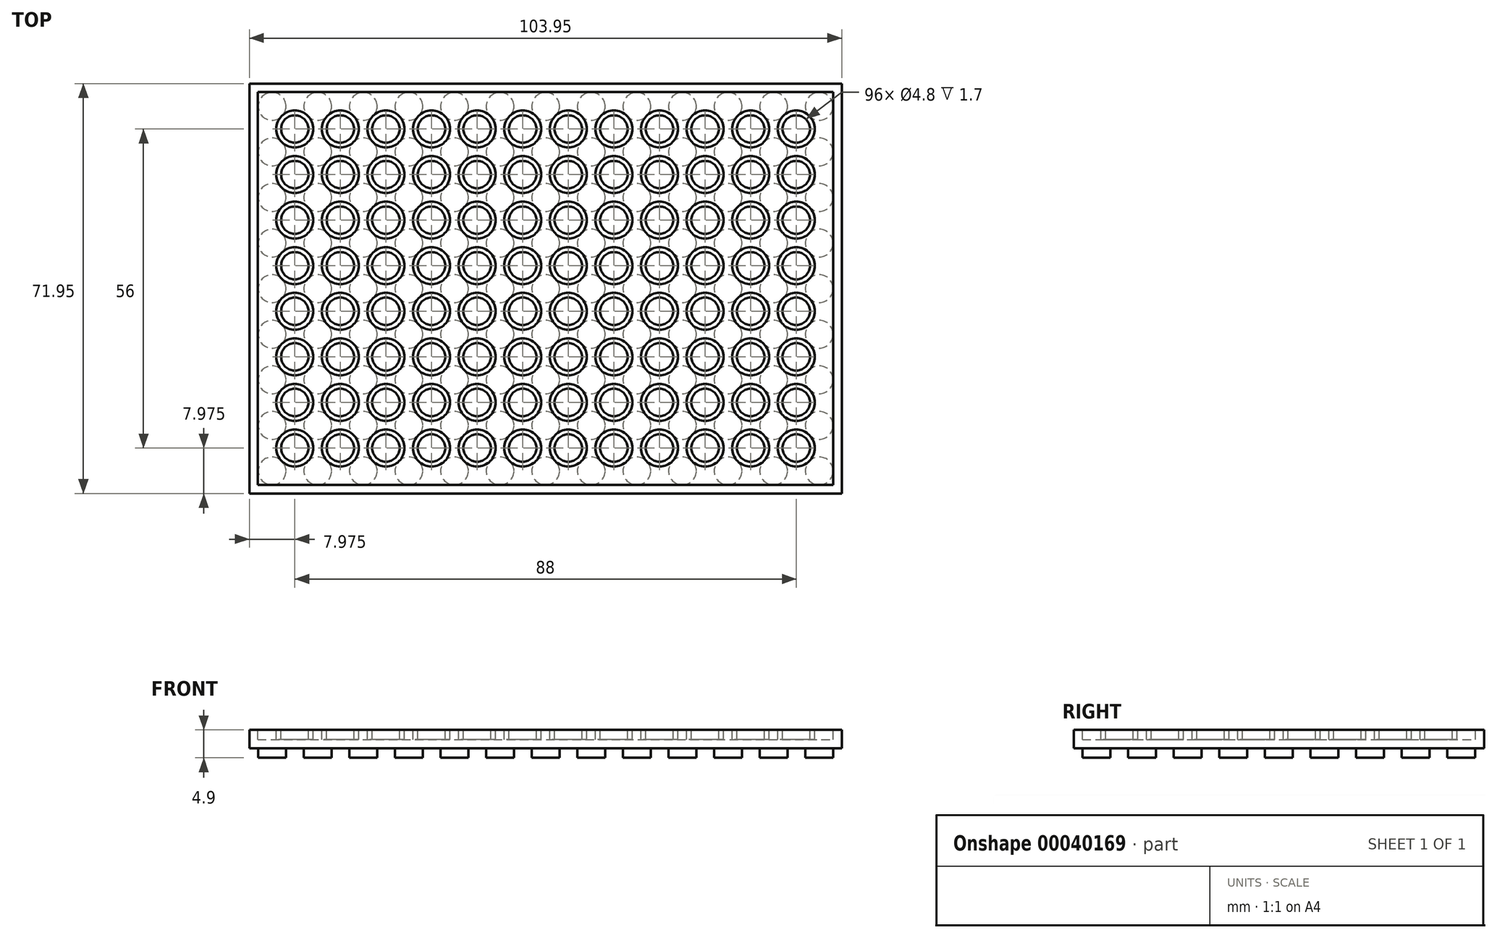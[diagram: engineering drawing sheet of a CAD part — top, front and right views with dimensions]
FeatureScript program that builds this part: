
annotation { "Feature Type Name" : "Feature", "Feature Type Description" : "" }
export const myFeature = defineFeature(function(context is Context, id is Id, definition is map)
    precondition{}
    {
        {
            var Q0;
            Q0=qCreatedBy(makeId("Top.planeOp"),FACE);
            var sketch = newSketch(context, id + "F0", { "sketchPlane" : qUnion([Q0])});
            skLineSegment(sketch, "E0.bottom", {"start": v(0, 0) * mm, "end": v(-103.95, 0) * mm});
            skLineSegment(sketch, "E0.top", {"start": v(0, 71.95) * mm, "end": v(-103.95, 71.95) * mm});
            skLineSegment(sketch, "E0.left", {"start": v(0, 0) * mm, "end": v(0, 71.95) * mm});
            skLineSegment(sketch, "E0.right", {"start": v(-103.95, 0) * mm, "end": v(-103.95, 71.95) * mm});
            skSolve(sketch);
        }
        {
            var Q0;
            Q0=makeQuery(id+"F0.imprint","IMPRINT",FACE,{"disambiguationData":[TD([[makeQuery(id+"F0.imprint","IMPRINT",EDGE,{"derivedFrom":sQuery(id+"F0.wireOp",EDGE,"E0.bottom")}),-1.0]])]});
            extrude(context, id + "F1", {"entities" : qUnion([Q0]), "oppositeDirection" : true, "depth" : 3.2 * mm});
        }
        {
            var Q0;
            Q0=qCreatedBy(makeId("Top.planeOp"),FACE);
            var sketch = newSketch(context, id + "F2", { "sketchPlane" : qUnion([Q0])});
            skLineSegment(sketch, "E1.bottom", {"start": v(-102.47, 1.47) * mm, "end": v(-1.47, 1.48) * mm});
            skLineSegment(sketch, "E1.top", {"start": v(-102.48, 70.47) * mm, "end": v(-1.48, 70.47) * mm});
            skLineSegment(sketch, "E1.left", {"start": v(-102.47, 1.47) * mm, "end": v(-102.48, 70.47) * mm});
            skLineSegment(sketch, "E1.right", {"start": v(-1.47, 1.48) * mm, "end": v(-1.48, 70.47) * mm});
            skCircle(sketch, "E2", {"center": v(-7.97, 7.98) * mm, "radius": 3.25 * mm});
            skCircle(sketch, "E3.0.1.0", {"center": v(-7.97, 15.98) * mm, "radius": 3.25 * mm});
            skCircle(sketch, "E3.0.2.0", {"center": v(-7.97, 23.98) * mm, "radius": 3.25 * mm});
            skCircle(sketch, "E3.0.3.0", {"center": v(-7.97, 31.98) * mm, "radius": 3.25 * mm});
            skCircle(sketch, "E3.0.4.0", {"center": v(-7.97, 39.98) * mm, "radius": 3.25 * mm});
            skCircle(sketch, "E3.0.5.0", {"center": v(-7.97, 47.98) * mm, "radius": 3.25 * mm});
            skCircle(sketch, "E3.0.6.0", {"center": v(-7.97, 55.98) * mm, "radius": 3.25 * mm});
            skCircle(sketch, "E3.0.7.0", {"center": v(-7.97, 63.98) * mm, "radius": 3.25 * mm});
            skCircle(sketch, "E3.1.0.0", {"center": v(-15.97, 7.98) * mm, "radius": 3.25 * mm});
            skCircle(sketch, "E3.1.1.0", {"center": v(-15.97, 15.98) * mm, "radius": 3.25 * mm});
            skCircle(sketch, "E3.1.2.0", {"center": v(-15.97, 23.98) * mm, "radius": 3.25 * mm});
            skCircle(sketch, "E3.1.3.0", {"center": v(-15.97, 31.98) * mm, "radius": 3.25 * mm});
            skCircle(sketch, "E3.1.4.0", {"center": v(-15.97, 39.98) * mm, "radius": 3.25 * mm});
            skCircle(sketch, "E3.1.5.0", {"center": v(-15.97, 47.98) * mm, "radius": 3.25 * mm});
            skCircle(sketch, "E3.1.6.0", {"center": v(-15.97, 55.98) * mm, "radius": 3.25 * mm});
            skCircle(sketch, "E3.1.7.0", {"center": v(-15.97, 63.98) * mm, "radius": 3.25 * mm});
            skCircle(sketch, "E3.2.0.0", {"center": v(-23.97, 7.98) * mm, "radius": 3.25 * mm});
            skCircle(sketch, "E3.2.1.0", {"center": v(-23.97, 15.98) * mm, "radius": 3.25 * mm});
            skCircle(sketch, "E3.2.2.0", {"center": v(-23.97, 23.98) * mm, "radius": 3.25 * mm});
            skCircle(sketch, "E3.2.3.0", {"center": v(-23.97, 31.98) * mm, "radius": 3.25 * mm});
            skCircle(sketch, "E3.2.4.0", {"center": v(-23.97, 39.98) * mm, "radius": 3.25 * mm});
            skCircle(sketch, "E3.2.5.0", {"center": v(-23.97, 47.98) * mm, "radius": 3.25 * mm});
            skCircle(sketch, "E3.2.6.0", {"center": v(-23.97, 55.98) * mm, "radius": 3.25 * mm});
            skCircle(sketch, "E3.2.7.0", {"center": v(-23.97, 63.98) * mm, "radius": 3.25 * mm});
            skCircle(sketch, "E3.3.0.0", {"center": v(-31.97, 7.98) * mm, "radius": 3.25 * mm});
            skCircle(sketch, "E3.3.1.0", {"center": v(-31.97, 15.98) * mm, "radius": 3.25 * mm});
            skCircle(sketch, "E3.3.2.0", {"center": v(-31.97, 23.98) * mm, "radius": 3.25 * mm});
            skCircle(sketch, "E3.3.3.0", {"center": v(-31.97, 31.98) * mm, "radius": 3.25 * mm});
            skCircle(sketch, "E3.3.4.0", {"center": v(-31.97, 39.98) * mm, "radius": 3.25 * mm});
            skCircle(sketch, "E3.3.5.0", {"center": v(-31.97, 47.98) * mm, "radius": 3.25 * mm});
            skCircle(sketch, "E3.3.6.0", {"center": v(-31.97, 55.98) * mm, "radius": 3.25 * mm});
            skCircle(sketch, "E3.3.7.0", {"center": v(-31.97, 63.98) * mm, "radius": 3.25 * mm});
            skCircle(sketch, "E3.4.0.0", {"center": v(-39.97, 7.98) * mm, "radius": 3.25 * mm});
            skCircle(sketch, "E3.4.1.0", {"center": v(-39.97, 15.98) * mm, "radius": 3.25 * mm});
            skCircle(sketch, "E3.4.2.0", {"center": v(-39.97, 23.98) * mm, "radius": 3.25 * mm});
            skCircle(sketch, "E3.4.3.0", {"center": v(-39.97, 31.98) * mm, "radius": 3.25 * mm});
            skCircle(sketch, "E3.4.4.0", {"center": v(-39.97, 39.98) * mm, "radius": 3.25 * mm});
            skCircle(sketch, "E3.4.5.0", {"center": v(-39.97, 47.98) * mm, "radius": 3.25 * mm});
            skCircle(sketch, "E3.4.6.0", {"center": v(-39.97, 55.98) * mm, "radius": 3.25 * mm});
            skCircle(sketch, "E3.4.7.0", {"center": v(-39.97, 63.98) * mm, "radius": 3.25 * mm});
            skCircle(sketch, "E3.5.0.0", {"center": v(-47.97, 7.98) * mm, "radius": 3.25 * mm});
            skCircle(sketch, "E3.5.1.0", {"center": v(-47.97, 15.98) * mm, "radius": 3.25 * mm});
            skCircle(sketch, "E3.5.2.0", {"center": v(-47.97, 23.98) * mm, "radius": 3.25 * mm});
            skCircle(sketch, "E3.5.3.0", {"center": v(-47.97, 31.98) * mm, "radius": 3.25 * mm});
            skCircle(sketch, "E3.5.4.0", {"center": v(-47.97, 39.98) * mm, "radius": 3.25 * mm});
            skCircle(sketch, "E3.5.5.0", {"center": v(-47.97, 47.98) * mm, "radius": 3.25 * mm});
            skCircle(sketch, "E3.5.6.0", {"center": v(-47.97, 55.98) * mm, "radius": 3.25 * mm});
            skCircle(sketch, "E3.5.7.0", {"center": v(-47.97, 63.98) * mm, "radius": 3.25 * mm});
            skCircle(sketch, "E3.6.0.0", {"center": v(-55.97, 7.98) * mm, "radius": 3.25 * mm});
            skCircle(sketch, "E3.6.1.0", {"center": v(-55.97, 15.98) * mm, "radius": 3.25 * mm});
            skCircle(sketch, "E3.6.2.0", {"center": v(-55.97, 23.98) * mm, "radius": 3.25 * mm});
            skCircle(sketch, "E3.6.3.0", {"center": v(-55.97, 31.98) * mm, "radius": 3.25 * mm});
            skCircle(sketch, "E3.6.4.0", {"center": v(-55.97, 39.98) * mm, "radius": 3.25 * mm});
            skCircle(sketch, "E3.6.5.0", {"center": v(-55.97, 47.98) * mm, "radius": 3.25 * mm});
            skCircle(sketch, "E3.6.6.0", {"center": v(-55.97, 55.98) * mm, "radius": 3.25 * mm});
            skCircle(sketch, "E3.6.7.0", {"center": v(-55.97, 63.98) * mm, "radius": 3.25 * mm});
            skCircle(sketch, "E3.7.0.0", {"center": v(-63.98, 7.98) * mm, "radius": 3.25 * mm});
            skCircle(sketch, "E3.7.1.0", {"center": v(-63.98, 15.98) * mm, "radius": 3.25 * mm});
            skCircle(sketch, "E3.7.2.0", {"center": v(-63.98, 23.98) * mm, "radius": 3.25 * mm});
            skCircle(sketch, "E3.7.3.0", {"center": v(-63.98, 31.98) * mm, "radius": 3.25 * mm});
            skCircle(sketch, "E3.7.4.0", {"center": v(-63.98, 39.98) * mm, "radius": 3.25 * mm});
            skCircle(sketch, "E3.7.5.0", {"center": v(-63.98, 47.98) * mm, "radius": 3.25 * mm});
            skCircle(sketch, "E3.7.6.0", {"center": v(-63.98, 55.98) * mm, "radius": 3.25 * mm});
            skCircle(sketch, "E3.7.7.0", {"center": v(-63.98, 63.98) * mm, "radius": 3.25 * mm});
            skCircle(sketch, "E3.8.0.0", {"center": v(-71.97, 7.98) * mm, "radius": 3.25 * mm});
            skCircle(sketch, "E3.8.1.0", {"center": v(-71.97, 15.98) * mm, "radius": 3.25 * mm});
            skCircle(sketch, "E3.8.2.0", {"center": v(-71.97, 23.98) * mm, "radius": 3.25 * mm});
            skCircle(sketch, "E3.8.3.0", {"center": v(-71.97, 31.98) * mm, "radius": 3.25 * mm});
            skCircle(sketch, "E3.8.4.0", {"center": v(-71.97, 39.98) * mm, "radius": 3.25 * mm});
            skCircle(sketch, "E3.8.5.0", {"center": v(-71.97, 47.98) * mm, "radius": 3.25 * mm});
            skCircle(sketch, "E3.8.6.0", {"center": v(-71.97, 55.98) * mm, "radius": 3.25 * mm});
            skCircle(sketch, "E3.8.7.0", {"center": v(-71.97, 63.98) * mm, "radius": 3.25 * mm});
            skCircle(sketch, "E3.9.0.0", {"center": v(-79.98, 7.98) * mm, "radius": 3.25 * mm});
            skCircle(sketch, "E3.9.1.0", {"center": v(-79.98, 15.98) * mm, "radius": 3.25 * mm});
            skCircle(sketch, "E3.9.2.0", {"center": v(-79.98, 23.98) * mm, "radius": 3.25 * mm});
            skCircle(sketch, "E3.9.3.0", {"center": v(-79.98, 31.98) * mm, "radius": 3.25 * mm});
            skCircle(sketch, "E3.9.4.0", {"center": v(-79.98, 39.98) * mm, "radius": 3.25 * mm});
            skCircle(sketch, "E3.9.5.0", {"center": v(-79.98, 47.98) * mm, "radius": 3.25 * mm});
            skCircle(sketch, "E3.9.6.0", {"center": v(-79.98, 55.98) * mm, "radius": 3.25 * mm});
            skCircle(sketch, "E3.9.7.0", {"center": v(-79.98, 63.98) * mm, "radius": 3.25 * mm});
            skCircle(sketch, "E3.10.0.0", {"center": v(-87.97, 7.98) * mm, "radius": 3.25 * mm});
            skCircle(sketch, "E3.10.1.0", {"center": v(-87.97, 15.98) * mm, "radius": 3.25 * mm});
            skCircle(sketch, "E3.10.2.0", {"center": v(-87.97, 23.98) * mm, "radius": 3.25 * mm});
            skCircle(sketch, "E3.10.3.0", {"center": v(-87.97, 31.98) * mm, "radius": 3.25 * mm});
            skCircle(sketch, "E3.10.4.0", {"center": v(-87.97, 39.98) * mm, "radius": 3.25 * mm});
            skCircle(sketch, "E3.10.5.0", {"center": v(-87.97, 47.98) * mm, "radius": 3.25 * mm});
            skCircle(sketch, "E3.10.6.0", {"center": v(-87.97, 55.98) * mm, "radius": 3.25 * mm});
            skCircle(sketch, "E3.10.7.0", {"center": v(-87.97, 63.98) * mm, "radius": 3.25 * mm});
            skCircle(sketch, "E3.11.0.0", {"center": v(-95.97, 7.98) * mm, "radius": 3.25 * mm});
            skCircle(sketch, "E3.11.1.0", {"center": v(-95.97, 15.98) * mm, "radius": 3.25 * mm});
            skCircle(sketch, "E3.11.2.0", {"center": v(-95.97, 23.98) * mm, "radius": 3.25 * mm});
            skCircle(sketch, "E3.11.3.0", {"center": v(-95.97, 31.98) * mm, "radius": 3.25 * mm});
            skCircle(sketch, "E3.11.4.0", {"center": v(-95.97, 39.98) * mm, "radius": 3.25 * mm});
            skCircle(sketch, "E3.11.5.0", {"center": v(-95.97, 47.98) * mm, "radius": 3.25 * mm});
            skCircle(sketch, "E3.11.6.0", {"center": v(-95.97, 55.98) * mm, "radius": 3.25 * mm});
            skCircle(sketch, "E3.11.7.0", {"center": v(-95.97, 63.98) * mm, "radius": 3.25 * mm});
            skLineSegment(sketch, "E3.direction1", {"start": v(-7.97, 7.98) * mm, "end": v(-15.97, 7.98) * mm, "construction": true});
            skLineSegment(sketch, "E3.direction2", {"start": v(-7.97, 7.98) * mm, "end": v(-7.97, 15.98) * mm, "construction": true});
            skSolve(sketch);
        }
        {
            var Q0;
            Q0=qCreatedBy(makeId("Top.planeOp"),FACE);
            var sketch = newSketch(context, id + "F3", { "sketchPlane" : qUnion([Q0])});
            skCircle(sketch, "E4", {"center": v(-7.97, 7.98) * mm, "radius": 2.4 * mm});
            skCircle(sketch, "E5.0.1.0", {"center": v(-7.97, 15.98) * mm, "radius": 2.4 * mm});
            skCircle(sketch, "E5.0.2.0", {"center": v(-7.97, 23.98) * mm, "radius": 2.4 * mm});
            skCircle(sketch, "E5.0.3.0", {"center": v(-7.97, 31.98) * mm, "radius": 2.4 * mm});
            skCircle(sketch, "E5.0.4.0", {"center": v(-7.97, 39.98) * mm, "radius": 2.4 * mm});
            skCircle(sketch, "E5.0.5.0", {"center": v(-7.97, 47.98) * mm, "radius": 2.4 * mm});
            skCircle(sketch, "E5.0.6.0", {"center": v(-7.97, 55.98) * mm, "radius": 2.4 * mm});
            skCircle(sketch, "E5.0.7.0", {"center": v(-7.97, 63.98) * mm, "radius": 2.4 * mm});
            skCircle(sketch, "E5.1.0.0", {"center": v(-15.97, 7.98) * mm, "radius": 2.4 * mm});
            skCircle(sketch, "E5.1.1.0", {"center": v(-15.97, 15.98) * mm, "radius": 2.4 * mm});
            skCircle(sketch, "E5.1.2.0", {"center": v(-15.97, 23.98) * mm, "radius": 2.4 * mm});
            skCircle(sketch, "E5.1.3.0", {"center": v(-15.97, 31.98) * mm, "radius": 2.4 * mm});
            skCircle(sketch, "E5.1.4.0", {"center": v(-15.97, 39.98) * mm, "radius": 2.4 * mm});
            skCircle(sketch, "E5.1.5.0", {"center": v(-15.97, 47.98) * mm, "radius": 2.4 * mm});
            skCircle(sketch, "E5.1.6.0", {"center": v(-15.97, 55.98) * mm, "radius": 2.4 * mm});
            skCircle(sketch, "E5.1.7.0", {"center": v(-15.97, 63.98) * mm, "radius": 2.4 * mm});
            skCircle(sketch, "E5.2.0.0", {"center": v(-23.97, 7.98) * mm, "radius": 2.4 * mm});
            skCircle(sketch, "E5.2.1.0", {"center": v(-23.97, 15.98) * mm, "radius": 2.4 * mm});
            skCircle(sketch, "E5.2.2.0", {"center": v(-23.97, 23.98) * mm, "radius": 2.4 * mm});
            skCircle(sketch, "E5.2.3.0", {"center": v(-23.97, 31.98) * mm, "radius": 2.4 * mm});
            skCircle(sketch, "E5.2.4.0", {"center": v(-23.97, 39.98) * mm, "radius": 2.4 * mm});
            skCircle(sketch, "E5.2.5.0", {"center": v(-23.97, 47.98) * mm, "radius": 2.4 * mm});
            skCircle(sketch, "E5.2.6.0", {"center": v(-23.97, 55.98) * mm, "radius": 2.4 * mm});
            skCircle(sketch, "E5.2.7.0", {"center": v(-23.97, 63.98) * mm, "radius": 2.4 * mm});
            skCircle(sketch, "E5.3.0.0", {"center": v(-31.97, 7.98) * mm, "radius": 2.4 * mm});
            skCircle(sketch, "E5.3.1.0", {"center": v(-31.97, 15.98) * mm, "radius": 2.4 * mm});
            skCircle(sketch, "E5.3.2.0", {"center": v(-31.97, 23.98) * mm, "radius": 2.4 * mm});
            skCircle(sketch, "E5.3.3.0", {"center": v(-31.97, 31.98) * mm, "radius": 2.4 * mm});
            skCircle(sketch, "E5.3.4.0", {"center": v(-31.97, 39.98) * mm, "radius": 2.4 * mm});
            skCircle(sketch, "E5.3.5.0", {"center": v(-31.97, 47.98) * mm, "radius": 2.4 * mm});
            skCircle(sketch, "E5.3.6.0", {"center": v(-31.97, 55.98) * mm, "radius": 2.4 * mm});
            skCircle(sketch, "E5.3.7.0", {"center": v(-31.97, 63.98) * mm, "radius": 2.4 * mm});
            skCircle(sketch, "E5.4.0.0", {"center": v(-39.97, 7.98) * mm, "radius": 2.4 * mm});
            skCircle(sketch, "E5.4.1.0", {"center": v(-39.97, 15.98) * mm, "radius": 2.4 * mm});
            skCircle(sketch, "E5.4.2.0", {"center": v(-39.97, 23.98) * mm, "radius": 2.4 * mm});
            skCircle(sketch, "E5.4.3.0", {"center": v(-39.97, 31.98) * mm, "radius": 2.4 * mm});
            skCircle(sketch, "E5.4.4.0", {"center": v(-39.97, 39.98) * mm, "radius": 2.4 * mm});
            skCircle(sketch, "E5.4.5.0", {"center": v(-39.97, 47.98) * mm, "radius": 2.4 * mm});
            skCircle(sketch, "E5.4.6.0", {"center": v(-39.97, 55.98) * mm, "radius": 2.4 * mm});
            skCircle(sketch, "E5.4.7.0", {"center": v(-39.97, 63.98) * mm, "radius": 2.4 * mm});
            skCircle(sketch, "E5.5.0.0", {"center": v(-47.97, 7.98) * mm, "radius": 2.4 * mm});
            skCircle(sketch, "E5.5.1.0", {"center": v(-47.97, 15.98) * mm, "radius": 2.4 * mm});
            skCircle(sketch, "E5.5.2.0", {"center": v(-47.97, 23.98) * mm, "radius": 2.4 * mm});
            skCircle(sketch, "E5.5.3.0", {"center": v(-47.97, 31.98) * mm, "radius": 2.4 * mm});
            skCircle(sketch, "E5.5.4.0", {"center": v(-47.97, 39.98) * mm, "radius": 2.4 * mm});
            skCircle(sketch, "E5.5.5.0", {"center": v(-47.97, 47.98) * mm, "radius": 2.4 * mm});
            skCircle(sketch, "E5.5.6.0", {"center": v(-47.97, 55.98) * mm, "radius": 2.4 * mm});
            skCircle(sketch, "E5.5.7.0", {"center": v(-47.97, 63.98) * mm, "radius": 2.4 * mm});
            skCircle(sketch, "E5.6.0.0", {"center": v(-55.97, 7.98) * mm, "radius": 2.4 * mm});
            skCircle(sketch, "E5.6.1.0", {"center": v(-55.97, 15.98) * mm, "radius": 2.4 * mm});
            skCircle(sketch, "E5.6.2.0", {"center": v(-55.97, 23.98) * mm, "radius": 2.4 * mm});
            skCircle(sketch, "E5.6.3.0", {"center": v(-55.97, 31.98) * mm, "radius": 2.4 * mm});
            skCircle(sketch, "E5.6.4.0", {"center": v(-55.97, 39.98) * mm, "radius": 2.4 * mm});
            skCircle(sketch, "E5.6.5.0", {"center": v(-55.97, 47.98) * mm, "radius": 2.4 * mm});
            skCircle(sketch, "E5.6.6.0", {"center": v(-55.97, 55.98) * mm, "radius": 2.4 * mm});
            skCircle(sketch, "E5.6.7.0", {"center": v(-55.97, 63.98) * mm, "radius": 2.4 * mm});
            skCircle(sketch, "E5.7.0.0", {"center": v(-63.98, 7.98) * mm, "radius": 2.4 * mm});
            skCircle(sketch, "E5.7.1.0", {"center": v(-63.98, 15.98) * mm, "radius": 2.4 * mm});
            skCircle(sketch, "E5.7.2.0", {"center": v(-63.98, 23.98) * mm, "radius": 2.4 * mm});
            skCircle(sketch, "E5.7.3.0", {"center": v(-63.98, 31.98) * mm, "radius": 2.4 * mm});
            skCircle(sketch, "E5.7.4.0", {"center": v(-63.98, 39.98) * mm, "radius": 2.4 * mm});
            skCircle(sketch, "E5.7.5.0", {"center": v(-63.98, 47.98) * mm, "radius": 2.4 * mm});
            skCircle(sketch, "E5.7.6.0", {"center": v(-63.98, 55.98) * mm, "radius": 2.4 * mm});
            skCircle(sketch, "E5.7.7.0", {"center": v(-63.98, 63.98) * mm, "radius": 2.4 * mm});
            skCircle(sketch, "E5.8.0.0", {"center": v(-71.97, 7.98) * mm, "radius": 2.4 * mm});
            skCircle(sketch, "E5.8.1.0", {"center": v(-71.97, 15.98) * mm, "radius": 2.4 * mm});
            skCircle(sketch, "E5.8.2.0", {"center": v(-71.97, 23.98) * mm, "radius": 2.4 * mm});
            skCircle(sketch, "E5.8.3.0", {"center": v(-71.97, 31.98) * mm, "radius": 2.4 * mm});
            skCircle(sketch, "E5.8.4.0", {"center": v(-71.97, 39.98) * mm, "radius": 2.4 * mm});
            skCircle(sketch, "E5.8.5.0", {"center": v(-71.97, 47.98) * mm, "radius": 2.4 * mm});
            skCircle(sketch, "E5.8.6.0", {"center": v(-71.97, 55.98) * mm, "radius": 2.4 * mm});
            skCircle(sketch, "E5.8.7.0", {"center": v(-71.97, 63.98) * mm, "radius": 2.4 * mm});
            skCircle(sketch, "E5.9.0.0", {"center": v(-79.98, 7.98) * mm, "radius": 2.4 * mm});
            skCircle(sketch, "E5.9.1.0", {"center": v(-79.98, 15.98) * mm, "radius": 2.4 * mm});
            skCircle(sketch, "E5.9.2.0", {"center": v(-79.98, 23.98) * mm, "radius": 2.4 * mm});
            skCircle(sketch, "E5.9.3.0", {"center": v(-79.98, 31.98) * mm, "radius": 2.4 * mm});
            skCircle(sketch, "E5.9.4.0", {"center": v(-79.98, 39.98) * mm, "radius": 2.4 * mm});
            skCircle(sketch, "E5.9.5.0", {"center": v(-79.98, 47.98) * mm, "radius": 2.4 * mm});
            skCircle(sketch, "E5.9.6.0", {"center": v(-79.98, 55.98) * mm, "radius": 2.4 * mm});
            skCircle(sketch, "E5.9.7.0", {"center": v(-79.98, 63.98) * mm, "radius": 2.4 * mm});
            skCircle(sketch, "E5.10.0.0", {"center": v(-87.97, 7.98) * mm, "radius": 2.4 * mm});
            skCircle(sketch, "E5.10.1.0", {"center": v(-87.97, 15.98) * mm, "radius": 2.4 * mm});
            skCircle(sketch, "E5.10.2.0", {"center": v(-87.97, 23.98) * mm, "radius": 2.4 * mm});
            skCircle(sketch, "E5.10.3.0", {"center": v(-87.97, 31.98) * mm, "radius": 2.4 * mm});
            skCircle(sketch, "E5.10.4.0", {"center": v(-87.97, 39.98) * mm, "radius": 2.4 * mm});
            skCircle(sketch, "E5.10.5.0", {"center": v(-87.97, 47.98) * mm, "radius": 2.4 * mm});
            skCircle(sketch, "E5.10.6.0", {"center": v(-87.97, 55.98) * mm, "radius": 2.4 * mm});
            skCircle(sketch, "E5.10.7.0", {"center": v(-87.97, 63.98) * mm, "radius": 2.4 * mm});
            skCircle(sketch, "E5.11.0.0", {"center": v(-95.97, 7.98) * mm, "radius": 2.4 * mm});
            skCircle(sketch, "E5.11.1.0", {"center": v(-95.97, 15.98) * mm, "radius": 2.4 * mm});
            skCircle(sketch, "E5.11.2.0", {"center": v(-95.97, 23.98) * mm, "radius": 2.4 * mm});
            skCircle(sketch, "E5.11.3.0", {"center": v(-95.97, 31.98) * mm, "radius": 2.4 * mm});
            skCircle(sketch, "E5.11.4.0", {"center": v(-95.97, 39.98) * mm, "radius": 2.4 * mm});
            skCircle(sketch, "E5.11.5.0", {"center": v(-95.97, 47.98) * mm, "radius": 2.4 * mm});
            skCircle(sketch, "E5.11.6.0", {"center": v(-95.97, 55.98) * mm, "radius": 2.4 * mm});
            skCircle(sketch, "E5.11.7.0", {"center": v(-95.97, 63.98) * mm, "radius": 2.4 * mm});
            skLineSegment(sketch, "E5.direction1", {"start": v(-7.97, 7.98) * mm, "end": v(-15.97, 7.98) * mm, "construction": true});
            skLineSegment(sketch, "E5.direction2", {"start": v(-7.97, 7.98) * mm, "end": v(-7.97, 15.98) * mm, "construction": true});
            skSolve(sketch);
        }
        {
            var Q0;
            Q0=qSketchRegion(id+"F3",true);
            var Q1;
            Q1=qSketchRegion(id+"F2",true);
            extrude(context, id + "F4", {"entities" : qUnion([Q0, Q1]), "operationType" : NewBodyOperationType.REMOVE, "oppositeDirection" : true, "depth" : 1.7 * mm});
        }
        {
            var Q0;
            Q0=makeQuery(id+"F1.opExtrude","CAP_FACE",FACE,{"disambiguationData":[OSD([sQuery(id+"F0.wireOp",EDGE,"E0.bottom"),sQuery(id+"F0.wireOp",EDGE,"E0.top"),sQuery(id+"F0.wireOp",EDGE,"E0.left"),sQuery(id+"F0.wireOp",EDGE,"E0.right")])],"isStart":false});
            var sketch = newSketch(context, id + "F5", { "sketchPlane" : qUnion([Q0])});
            skCircle(sketch, "E6", {"center": v(-99.95, -67.95) * mm, "radius": 2.45 * mm});
            skCircle(sketch, "E7.0.1.0", {"center": v(-99.95, -59.95) * mm, "radius": 2.45 * mm});
            skCircle(sketch, "E7.0.2.0", {"center": v(-99.95, -51.95) * mm, "radius": 2.45 * mm});
            skCircle(sketch, "E7.0.3.0", {"center": v(-99.95, -43.95) * mm, "radius": 2.45 * mm});
            skCircle(sketch, "E7.0.4.0", {"center": v(-99.95, -35.95) * mm, "radius": 2.45 * mm});
            skCircle(sketch, "E7.0.5.0", {"center": v(-99.95, -27.95) * mm, "radius": 2.45 * mm});
            skCircle(sketch, "E7.0.6.0", {"center": v(-99.95, -19.95) * mm, "radius": 2.45 * mm});
            skCircle(sketch, "E7.0.7.0", {"center": v(-99.95, -11.95) * mm, "radius": 2.45 * mm});
            skCircle(sketch, "E7.1.0.0", {"center": v(-91.95, -67.95) * mm, "radius": 2.45 * mm});
            skCircle(sketch, "E7.1.1.0", {"center": v(-91.95, -59.95) * mm, "radius": 2.45 * mm});
            skCircle(sketch, "E7.1.2.0", {"center": v(-91.95, -51.95) * mm, "radius": 2.45 * mm});
            skCircle(sketch, "E7.1.3.0", {"center": v(-91.95, -43.95) * mm, "radius": 2.45 * mm});
            skCircle(sketch, "E7.1.4.0", {"center": v(-91.95, -35.95) * mm, "radius": 2.45 * mm});
            skCircle(sketch, "E7.1.5.0", {"center": v(-91.95, -27.95) * mm, "radius": 2.45 * mm});
            skCircle(sketch, "E7.1.6.0", {"center": v(-91.95, -19.95) * mm, "radius": 2.45 * mm});
            skCircle(sketch, "E7.1.7.0", {"center": v(-91.95, -11.95) * mm, "radius": 2.45 * mm});
            skCircle(sketch, "E7.2.0.0", {"center": v(-83.95, -67.95) * mm, "radius": 2.45 * mm});
            skCircle(sketch, "E7.2.1.0", {"center": v(-83.95, -59.95) * mm, "radius": 2.45 * mm});
            skCircle(sketch, "E7.2.2.0", {"center": v(-83.95, -51.95) * mm, "radius": 2.45 * mm});
            skCircle(sketch, "E7.2.3.0", {"center": v(-83.95, -43.95) * mm, "radius": 2.45 * mm});
            skCircle(sketch, "E7.2.4.0", {"center": v(-83.95, -35.95) * mm, "radius": 2.45 * mm});
            skCircle(sketch, "E7.2.5.0", {"center": v(-83.95, -27.95) * mm, "radius": 2.45 * mm});
            skCircle(sketch, "E7.2.6.0", {"center": v(-83.95, -19.95) * mm, "radius": 2.45 * mm});
            skCircle(sketch, "E7.2.7.0", {"center": v(-83.95, -11.95) * mm, "radius": 2.45 * mm});
            skCircle(sketch, "E7.3.0.0", {"center": v(-75.95, -67.95) * mm, "radius": 2.45 * mm});
            skCircle(sketch, "E7.3.1.0", {"center": v(-75.95, -59.95) * mm, "radius": 2.45 * mm});
            skCircle(sketch, "E7.3.2.0", {"center": v(-75.95, -51.95) * mm, "radius": 2.45 * mm});
            skCircle(sketch, "E7.3.3.0", {"center": v(-75.95, -43.95) * mm, "radius": 2.45 * mm});
            skCircle(sketch, "E7.3.4.0", {"center": v(-75.95, -35.95) * mm, "radius": 2.45 * mm});
            skCircle(sketch, "E7.3.5.0", {"center": v(-75.95, -27.95) * mm, "radius": 2.45 * mm});
            skCircle(sketch, "E7.3.6.0", {"center": v(-75.95, -19.95) * mm, "radius": 2.45 * mm});
            skCircle(sketch, "E7.3.7.0", {"center": v(-75.95, -11.95) * mm, "radius": 2.45 * mm});
            skCircle(sketch, "E7.4.0.0", {"center": v(-67.95, -67.95) * mm, "radius": 2.45 * mm});
            skCircle(sketch, "E7.4.1.0", {"center": v(-67.95, -59.95) * mm, "radius": 2.45 * mm});
            skCircle(sketch, "E7.4.2.0", {"center": v(-67.95, -51.95) * mm, "radius": 2.45 * mm});
            skCircle(sketch, "E7.4.3.0", {"center": v(-67.95, -43.95) * mm, "radius": 2.45 * mm});
            skCircle(sketch, "E7.4.4.0", {"center": v(-67.95, -35.95) * mm, "radius": 2.45 * mm});
            skCircle(sketch, "E7.4.5.0", {"center": v(-67.95, -27.95) * mm, "radius": 2.45 * mm});
            skCircle(sketch, "E7.4.6.0", {"center": v(-67.95, -19.95) * mm, "radius": 2.45 * mm});
            skCircle(sketch, "E7.4.7.0", {"center": v(-67.95, -11.95) * mm, "radius": 2.45 * mm});
            skCircle(sketch, "E7.5.0.0", {"center": v(-59.95, -67.95) * mm, "radius": 2.45 * mm});
            skCircle(sketch, "E7.5.1.0", {"center": v(-59.95, -59.95) * mm, "radius": 2.45 * mm});
            skCircle(sketch, "E7.5.2.0", {"center": v(-59.95, -51.95) * mm, "radius": 2.45 * mm});
            skCircle(sketch, "E7.5.3.0", {"center": v(-59.95, -43.95) * mm, "radius": 2.45 * mm});
            skCircle(sketch, "E7.5.4.0", {"center": v(-59.95, -35.95) * mm, "radius": 2.45 * mm});
            skCircle(sketch, "E7.5.5.0", {"center": v(-59.95, -27.95) * mm, "radius": 2.45 * mm});
            skCircle(sketch, "E7.5.6.0", {"center": v(-59.95, -19.95) * mm, "radius": 2.45 * mm});
            skCircle(sketch, "E7.5.7.0", {"center": v(-59.95, -11.95) * mm, "radius": 2.45 * mm});
            skCircle(sketch, "E7.6.0.0", {"center": v(-51.95, -67.95) * mm, "radius": 2.45 * mm});
            skCircle(sketch, "E7.6.1.0", {"center": v(-51.95, -59.95) * mm, "radius": 2.45 * mm});
            skCircle(sketch, "E7.6.2.0", {"center": v(-51.95, -51.95) * mm, "radius": 2.45 * mm});
            skCircle(sketch, "E7.6.3.0", {"center": v(-51.95, -43.95) * mm, "radius": 2.45 * mm});
            skCircle(sketch, "E7.6.4.0", {"center": v(-51.95, -35.95) * mm, "radius": 2.45 * mm});
            skCircle(sketch, "E7.6.5.0", {"center": v(-51.95, -27.95) * mm, "radius": 2.45 * mm});
            skCircle(sketch, "E7.6.6.0", {"center": v(-51.95, -19.95) * mm, "radius": 2.45 * mm});
            skCircle(sketch, "E7.6.7.0", {"center": v(-51.95, -11.95) * mm, "radius": 2.45 * mm});
            skCircle(sketch, "E7.7.0.0", {"center": v(-43.95, -67.95) * mm, "radius": 2.45 * mm});
            skCircle(sketch, "E7.7.1.0", {"center": v(-43.95, -59.95) * mm, "radius": 2.45 * mm});
            skCircle(sketch, "E7.7.2.0", {"center": v(-43.95, -51.95) * mm, "radius": 2.45 * mm});
            skCircle(sketch, "E7.7.3.0", {"center": v(-43.95, -43.95) * mm, "radius": 2.45 * mm});
            skCircle(sketch, "E7.7.4.0", {"center": v(-43.95, -35.95) * mm, "radius": 2.45 * mm});
            skCircle(sketch, "E7.7.5.0", {"center": v(-43.95, -27.95) * mm, "radius": 2.45 * mm});
            skCircle(sketch, "E7.7.6.0", {"center": v(-43.95, -19.95) * mm, "radius": 2.45 * mm});
            skCircle(sketch, "E7.7.7.0", {"center": v(-43.95, -11.95) * mm, "radius": 2.45 * mm});
            skCircle(sketch, "E7.8.0.0", {"center": v(-35.95, -67.95) * mm, "radius": 2.45 * mm});
            skCircle(sketch, "E7.8.1.0", {"center": v(-35.95, -59.95) * mm, "radius": 2.45 * mm});
            skCircle(sketch, "E7.8.2.0", {"center": v(-35.95, -51.95) * mm, "radius": 2.45 * mm});
            skCircle(sketch, "E7.8.3.0", {"center": v(-35.95, -43.95) * mm, "radius": 2.45 * mm});
            skCircle(sketch, "E7.8.4.0", {"center": v(-35.95, -35.95) * mm, "radius": 2.45 * mm});
            skCircle(sketch, "E7.8.5.0", {"center": v(-35.95, -27.95) * mm, "radius": 2.45 * mm});
            skCircle(sketch, "E7.8.6.0", {"center": v(-35.95, -19.95) * mm, "radius": 2.45 * mm});
            skCircle(sketch, "E7.8.7.0", {"center": v(-35.95, -11.95) * mm, "radius": 2.45 * mm});
            skCircle(sketch, "E7.9.0.0", {"center": v(-27.95, -67.95) * mm, "radius": 2.45 * mm});
            skCircle(sketch, "E7.9.1.0", {"center": v(-27.95, -59.95) * mm, "radius": 2.45 * mm});
            skCircle(sketch, "E7.9.2.0", {"center": v(-27.95, -51.95) * mm, "radius": 2.45 * mm});
            skCircle(sketch, "E7.9.3.0", {"center": v(-27.95, -43.95) * mm, "radius": 2.45 * mm});
            skCircle(sketch, "E7.9.4.0", {"center": v(-27.95, -35.95) * mm, "radius": 2.45 * mm});
            skCircle(sketch, "E7.9.5.0", {"center": v(-27.95, -27.95) * mm, "radius": 2.45 * mm});
            skCircle(sketch, "E7.9.6.0", {"center": v(-27.95, -19.95) * mm, "radius": 2.45 * mm});
            skCircle(sketch, "E7.9.7.0", {"center": v(-27.95, -11.95) * mm, "radius": 2.45 * mm});
            skCircle(sketch, "E7.10.0.0", {"center": v(-19.95, -67.95) * mm, "radius": 2.45 * mm});
            skCircle(sketch, "E7.10.1.0", {"center": v(-19.95, -59.95) * mm, "radius": 2.45 * mm});
            skCircle(sketch, "E7.10.2.0", {"center": v(-19.95, -51.95) * mm, "radius": 2.45 * mm});
            skCircle(sketch, "E7.10.3.0", {"center": v(-19.95, -43.95) * mm, "radius": 2.45 * mm});
            skCircle(sketch, "E7.10.4.0", {"center": v(-19.95, -35.95) * mm, "radius": 2.45 * mm});
            skCircle(sketch, "E7.10.5.0", {"center": v(-19.95, -27.95) * mm, "radius": 2.45 * mm});
            skCircle(sketch, "E7.10.6.0", {"center": v(-19.95, -19.95) * mm, "radius": 2.45 * mm});
            skCircle(sketch, "E7.10.7.0", {"center": v(-19.95, -11.95) * mm, "radius": 2.45 * mm});
            skCircle(sketch, "E7.11.0.0", {"center": v(-11.95, -67.95) * mm, "radius": 2.45 * mm});
            skCircle(sketch, "E7.11.1.0", {"center": v(-11.95, -59.95) * mm, "radius": 2.45 * mm});
            skCircle(sketch, "E7.11.2.0", {"center": v(-11.95, -51.95) * mm, "radius": 2.45 * mm});
            skCircle(sketch, "E7.11.3.0", {"center": v(-11.95, -43.95) * mm, "radius": 2.45 * mm});
            skCircle(sketch, "E7.11.4.0", {"center": v(-11.95, -35.95) * mm, "radius": 2.45 * mm});
            skCircle(sketch, "E7.11.5.0", {"center": v(-11.95, -27.95) * mm, "radius": 2.45 * mm});
            skCircle(sketch, "E7.11.6.0", {"center": v(-11.95, -19.95) * mm, "radius": 2.45 * mm});
            skCircle(sketch, "E7.11.7.0", {"center": v(-11.95, -11.95) * mm, "radius": 2.45 * mm});
            skCircle(sketch, "E7.12.0.0", {"center": v(-3.95, -67.95) * mm, "radius": 2.45 * mm});
            skCircle(sketch, "E7.12.1.0", {"center": v(-3.95, -59.95) * mm, "radius": 2.45 * mm});
            skCircle(sketch, "E7.12.2.0", {"center": v(-3.95, -51.95) * mm, "radius": 2.45 * mm});
            skCircle(sketch, "E7.12.3.0", {"center": v(-3.95, -43.95) * mm, "radius": 2.45 * mm});
            skCircle(sketch, "E7.12.4.0", {"center": v(-3.95, -35.95) * mm, "radius": 2.45 * mm});
            skCircle(sketch, "E7.12.5.0", {"center": v(-3.95, -27.95) * mm, "radius": 2.45 * mm});
            skCircle(sketch, "E7.12.6.0", {"center": v(-3.95, -19.95) * mm, "radius": 2.45 * mm});
            skCircle(sketch, "E7.12.7.0", {"center": v(-3.95, -11.95) * mm, "radius": 2.45 * mm});
            skLineSegment(sketch, "E7.direction1", {"start": v(-99.95, -67.95) * mm, "end": v(-91.95, -67.95) * mm, "construction": true});
            skLineSegment(sketch, "E7.direction2", {"start": v(-99.95, -67.95) * mm, "end": v(-99.95, -59.95) * mm, "construction": true});
            skCircle(sketch, "E8.0.0.8", {"center": v(-99.95, -3.95) * mm, "radius": 2.45 * mm});
            skCircle(sketch, "E8.0.1.8", {"center": v(-91.95, -3.95) * mm, "radius": 2.45 * mm});
            skCircle(sketch, "E8.0.2.8", {"center": v(-83.95, -3.95) * mm, "radius": 2.45 * mm});
            skCircle(sketch, "E8.0.3.8", {"center": v(-75.95, -3.95) * mm, "radius": 2.45 * mm});
            skCircle(sketch, "E8.0.4.8", {"center": v(-67.95, -3.95) * mm, "radius": 2.45 * mm});
            skCircle(sketch, "E8.0.5.8", {"center": v(-59.95, -3.95) * mm, "radius": 2.45 * mm});
            skCircle(sketch, "E8.0.6.8", {"center": v(-51.95, -3.95) * mm, "radius": 2.45 * mm});
            skCircle(sketch, "E8.0.7.8", {"center": v(-43.95, -3.95) * mm, "radius": 2.45 * mm});
            skCircle(sketch, "E8.0.8.8", {"center": v(-35.95, -3.95) * mm, "radius": 2.45 * mm});
            skCircle(sketch, "E8.0.9.8", {"center": v(-27.95, -3.95) * mm, "radius": 2.45 * mm});
            skCircle(sketch, "E8.0.10.8", {"center": v(-19.95, -3.95) * mm, "radius": 2.45 * mm});
            skCircle(sketch, "E8.0.11.8", {"center": v(-11.95, -3.95) * mm, "radius": 2.45 * mm});
            skCircle(sketch, "E8.0.12.8", {"center": v(-3.95, -3.95) * mm, "radius": 2.45 * mm});
            skSolve(sketch);
        }
        {
            var Q0;
            Q0=qSketchRegion(id+"F5",true);
            extrude(context, id + "F6", {"entities" : qUnion([Q0]), "operationType" : NewBodyOperationType.ADD, "depth" : 1.7 * mm});
        }
    });
